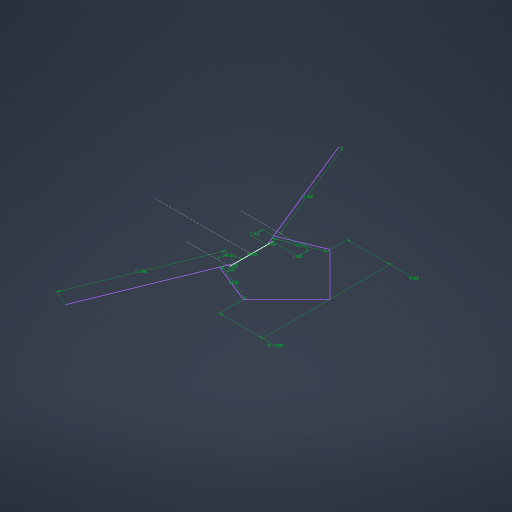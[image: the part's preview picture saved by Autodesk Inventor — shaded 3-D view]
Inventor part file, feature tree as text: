
AUTODESK INVENTOR PART (.ipt)
format: ipt  version: 2023 (Build 270158000, 158)  size: 180,736 bytes
history: native  units: in
note: dims shown in document units (in); Inventor stores cm internally (conversion verified against a paired STEP export)
features: sketch x1
ambient origin geometry x8: Origin, YZ Plane, XZ Plane, XY Plane, X Axis, Y Axis, Z Axis, Center Point
feature tree (1):
  sketch  "Sketch1"  dims[d0=4.0in d1=90.0deg d2=0.5in d3=0.5in d5=12.0in d6=4.0in d7=0.5in d10=1.0in d19=12.0in d20=4.0in d21=1.0in d28=4.0in d29=4.0in]
